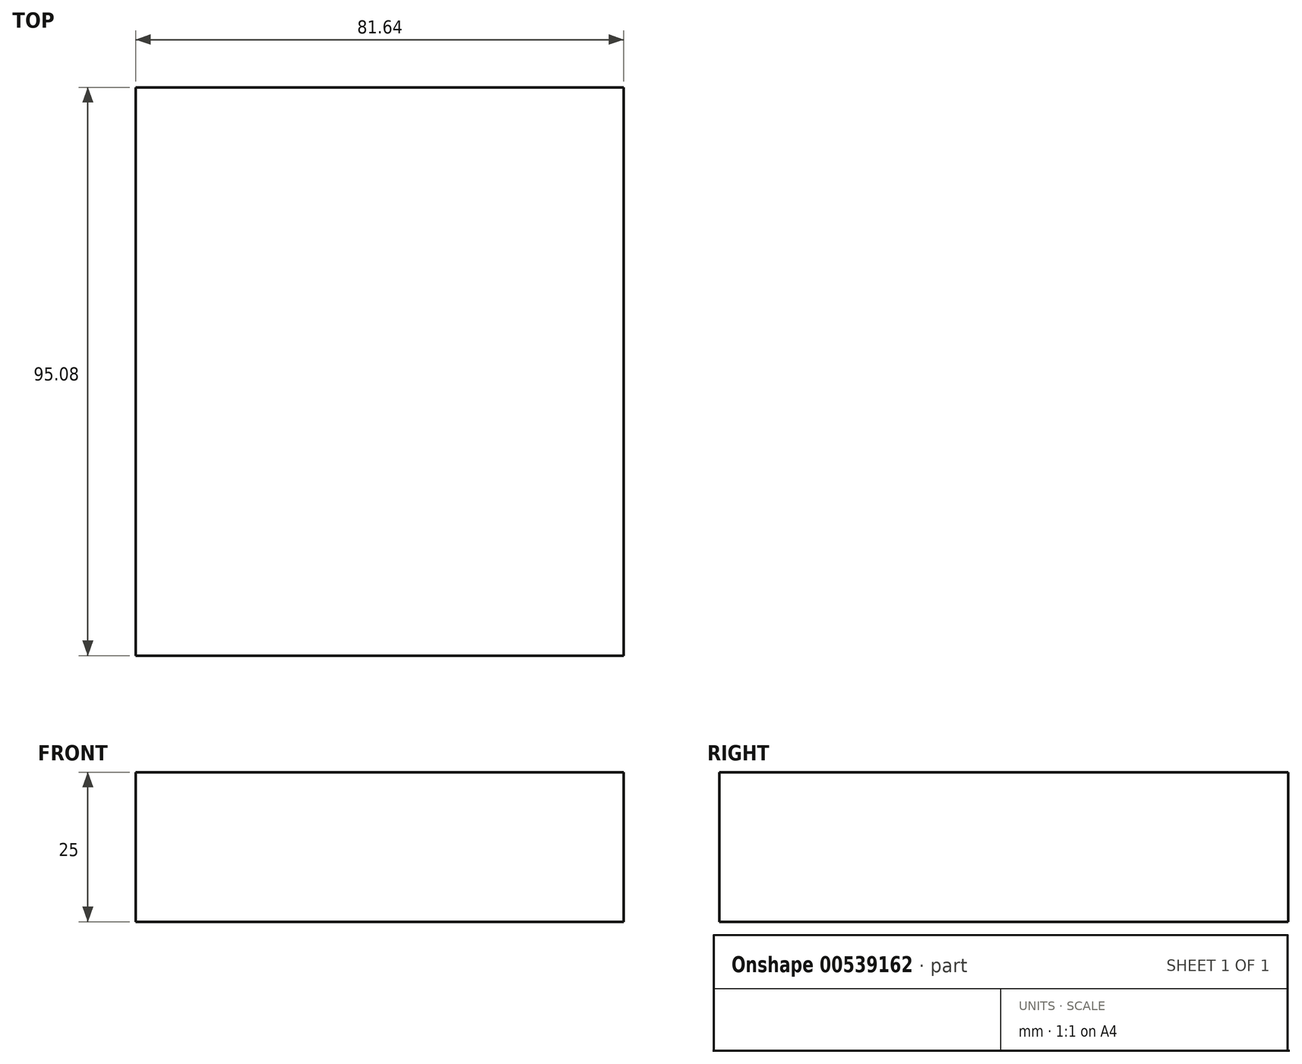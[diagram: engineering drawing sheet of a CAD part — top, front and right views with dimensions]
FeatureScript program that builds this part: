
annotation { "Feature Type Name" : "Feature", "Feature Type Description" : "" }
export const myFeature = defineFeature(function(context is Context, id is Id, definition is map)
    precondition{}
    {
        {
            var Q0;
            Q0=qCreatedBy(makeId("Top.planeOp"),FACE);
            var sketch = newSketch(context, id + "F0", { "sketchPlane" : qUnion([Q0])});
            skLineSegment(sketch, "E0.bottom", {"start": v(40.82, -45.3) * mm, "end": v(-40.82, -45.3) * mm});
            skLineSegment(sketch, "E0.top", {"start": v(40.82, 49.78) * mm, "end": v(-40.82, 49.78) * mm});
            skLineSegment(sketch, "E0.left", {"start": v(40.82, -45.3) * mm, "end": v(40.82, 49.78) * mm});
            skLineSegment(sketch, "E0.right", {"start": v(-40.82, -45.3) * mm, "end": v(-40.82, 49.78) * mm});
            skPoint(sketch, "E0.middle", {"position": v(0, 2.24) * mm});
            skSolve(sketch);
        }
        {
            var Q0;
            Q0 = qSketchRegion(id + "F0", true);
            extrude(context, id + "F1", {"entities" : qUnion([Q0]), "depth" : 25 * mm, "offsetDistance" : 25 * mm});
        }
    });
